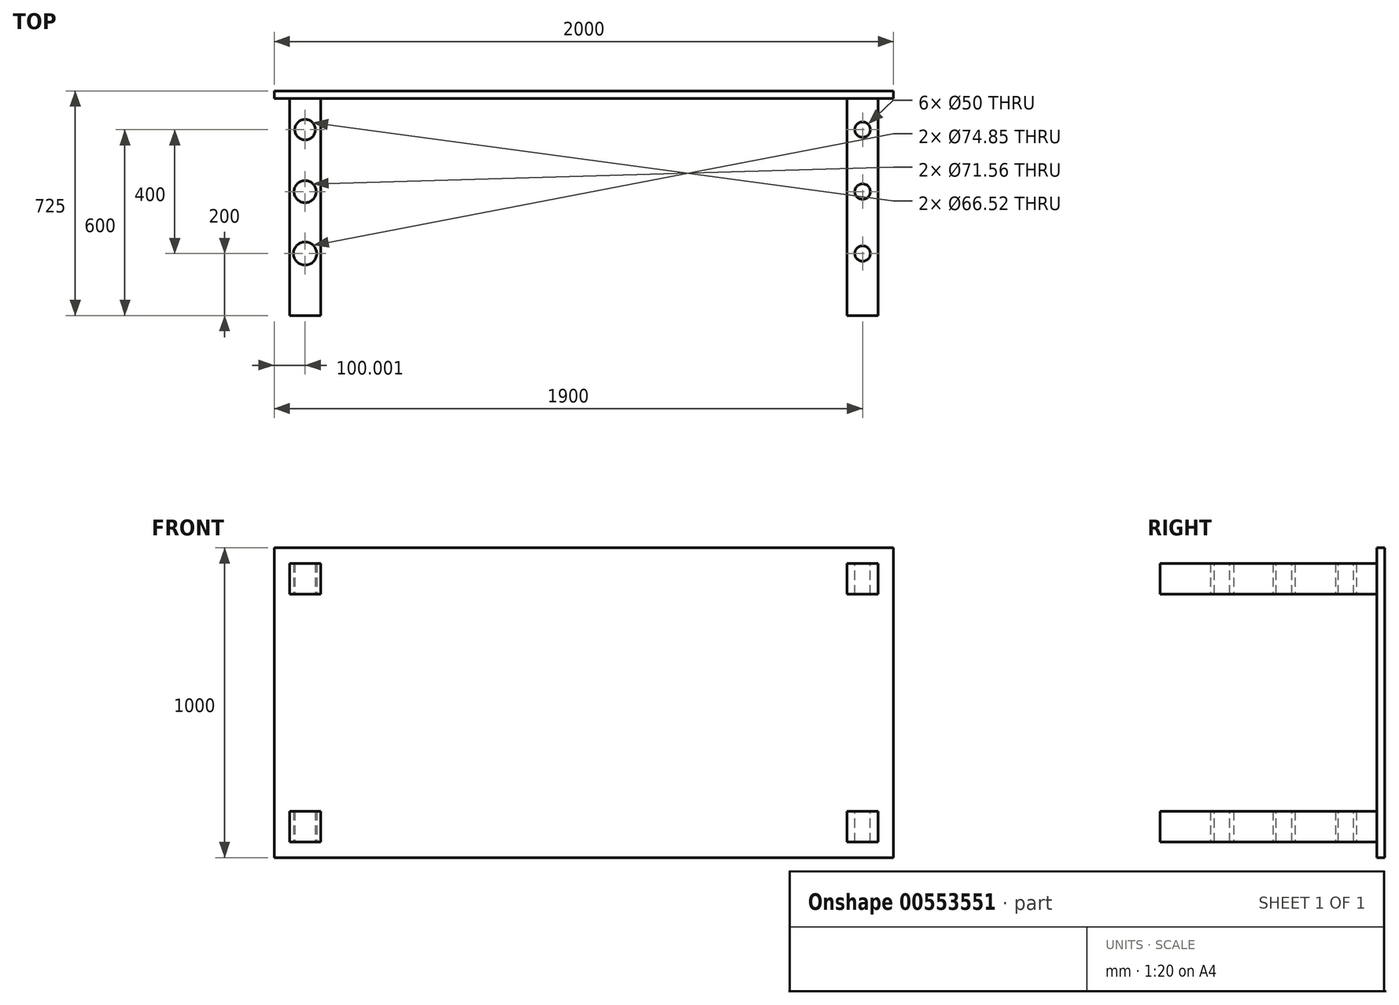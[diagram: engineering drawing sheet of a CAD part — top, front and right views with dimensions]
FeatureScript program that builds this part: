
annotation { "Feature Type Name" : "Feature", "Feature Type Description" : "" }
export const myFeature = defineFeature(function(context is Context, id is Id, definition is map)
    precondition{}
    {
        {
            var Q0;
            Q0=qCreatedBy(makeId("Front.planeOp"),FACE);
            var sketch = newSketch(context, id + "F0", { "sketchPlane" : qUnion([Q0])});
            skLineSegment(sketch, "E0.bottom", {"start": v(-1006.46, -488.64) * mm, "end": v(993.54, -488.64) * mm});
            skLineSegment(sketch, "E0.top", {"start": v(-1006.46, 511.36) * mm, "end": v(993.54, 511.36) * mm});
            skLineSegment(sketch, "E0.left", {"start": v(-1006.46, -488.64) * mm, "end": v(-1006.46, 511.36) * mm});
            skLineSegment(sketch, "E0.right", {"start": v(993.54, -488.64) * mm, "end": v(993.54, 511.36) * mm});
            skLineSegment(sketch, "E1.bottom", {"start": v(843.54, -438.64) * mm, "end": v(943.54, -438.64) * mm});
            skLineSegment(sketch, "E1.top", {"start": v(843.54, -338.64) * mm, "end": v(943.54, -338.64) * mm});
            skLineSegment(sketch, "E1.left", {"start": v(843.54, -438.64) * mm, "end": v(843.54, -338.64) * mm});
            skLineSegment(sketch, "E1.right", {"start": v(943.54, -438.64) * mm, "end": v(943.54, -338.64) * mm});
            skLineSegment(sketch, "E2.bottom", {"start": v(943.54, 461.36) * mm, "end": v(843.54, 461.36) * mm});
            skLineSegment(sketch, "E2.top", {"start": v(943.54, 361.36) * mm, "end": v(843.54, 361.36) * mm});
            skLineSegment(sketch, "E2.left", {"start": v(943.54, 461.36) * mm, "end": v(943.54, 361.36) * mm});
            skLineSegment(sketch, "E2.right", {"start": v(843.54, 461.36) * mm, "end": v(843.54, 361.36) * mm});
            skLineSegment(sketch, "E3.bottom", {"start": v(-956.46, 461.36) * mm, "end": v(-856.46, 461.36) * mm});
            skLineSegment(sketch, "E3.top", {"start": v(-956.46, 361.36) * mm, "end": v(-856.46, 361.36) * mm});
            skLineSegment(sketch, "E3.left", {"start": v(-956.46, 461.36) * mm, "end": v(-956.46, 361.36) * mm});
            skLineSegment(sketch, "E3.right", {"start": v(-856.46, 461.36) * mm, "end": v(-856.46, 361.36) * mm});
            skLineSegment(sketch, "E4.bottom", {"start": v(-956.46, -438.64) * mm, "end": v(-856.46, -438.64) * mm});
            skLineSegment(sketch, "E4.top", {"start": v(-956.46, -338.64) * mm, "end": v(-856.46, -338.64) * mm});
            skLineSegment(sketch, "E4.left", {"start": v(-956.46, -438.64) * mm, "end": v(-956.46, -338.64) * mm});
            skLineSegment(sketch, "E4.right", {"start": v(-856.46, -438.64) * mm, "end": v(-856.46, -338.64) * mm});
            skSolve(sketch);
        }
        {
            var Q0;
            Q0 = qSketchRegion(id + "F0", true);
            extrude(context, id + "F1", {"entities" : qUnion([Q0]), "depth" : 25 * mm, "offsetDistance" : 25 * mm});
        }
        {
            var Q0;
            Q0=makeQuery(id+"F0.imprint","IMPRINT",FACE,{"disambiguationData":[TD([[makeQuery(id+"F0.imprint","IMPRINT",EDGE,{"derivedFrom":sQuery(id+"F0.wireOp",EDGE,"E1.bottom")}),1.0]])]});
            var Q1;
            Q1=makeQuery(id+"F0.imprint","IMPRINT",FACE,{"disambiguationData":[TD([[makeQuery(id+"F0.imprint","IMPRINT",EDGE,{"derivedFrom":sQuery(id+"F0.wireOp",EDGE,"E4.bottom")}),1.0]])]});
            var Q2;
            Q2=makeQuery(id+"F0.imprint","IMPRINT",FACE,{"disambiguationData":[TD([[makeQuery(id+"F0.imprint","IMPRINT",EDGE,{"derivedFrom":sQuery(id+"F0.wireOp",EDGE,"E3.bottom")}),-1.0]])]});
            var Q3;
            Q3=makeQuery(id+"F0.imprint","IMPRINT",FACE,{"disambiguationData":[TD([[makeQuery(id+"F0.imprint","IMPRINT",EDGE,{"derivedFrom":sQuery(id+"F0.wireOp",EDGE,"E2.bottom")}),1.0]])]});
            extrude(context, id + "F2", {"entities" : qUnion([Q0, Q1, Q2, Q3]), "operationType" : NewBodyOperationType.ADD, "depth" : 725 * mm, "offsetDistance" : 25 * mm});
        }
        {
            var Q0;
            Q0=makeQuery(id+"F2.opExtrude","SWEPT_FACE",FACE,{"disambiguationData":[OSD([sQuery(id+"F0.wireOp",EDGE,"E4.bottom")])]});
            var sketch = newSketch(context, id + "F3", { "sketchPlane" : qUnion([Q0])});
            skCircle(sketch, "E5", {"center": v(-906.46, 125) * mm, "radius": 33.26 * mm});
            skCircle(sketch, "E6", {"center": v(-906.46, 325) * mm, "radius": 35.78 * mm});
            skCircle(sketch, "E7", {"center": v(-906.46, 525) * mm, "radius": 37.43 * mm});
            skSolve(sketch);
        }
        {
            var Q0;
            Q0 = qSketchRegion(id + "F3", true);
            extrude(context, id + "F4", {"entities" : qUnion([Q0]), "operationType" : NewBodyOperationType.REMOVE, "endBound" : BoundingType.THROUGH_ALL, "oppositeDirection" : true, "depth" : 25 * mm, "offsetDistance" : 25 * mm});
        }
        {
            var Q0;
            Q0=makeQuery(id+"F2.opExtrude","SWEPT_FACE",FACE,{"disambiguationData":[OSD([sQuery(id+"F0.wireOp",EDGE,"E2.bottom")])]});
            var sketch = newSketch(context, id + "F5", { "sketchPlane" : qUnion([Q0])});
            skCircle(sketch, "E8", {"center": v(893.54, -525) * mm, "radius": 25 * mm});
            skCircle(sketch, "E9", {"center": v(893.54, -325) * mm, "radius": 25 * mm});
            skCircle(sketch, "E10", {"center": v(893.54, -125) * mm, "radius": 25 * mm});
            skSolve(sketch);
        }
        {
            var Q0;
            Q0 = qSketchRegion(id + "F5", true);
            extrude(context, id + "F6", {"entities" : qUnion([Q0]), "operationType" : NewBodyOperationType.REMOVE, "endBound" : BoundingType.THROUGH_ALL, "oppositeDirection" : true, "depth" : 25 * mm, "offsetDistance" : 25 * mm});
        }
    });
